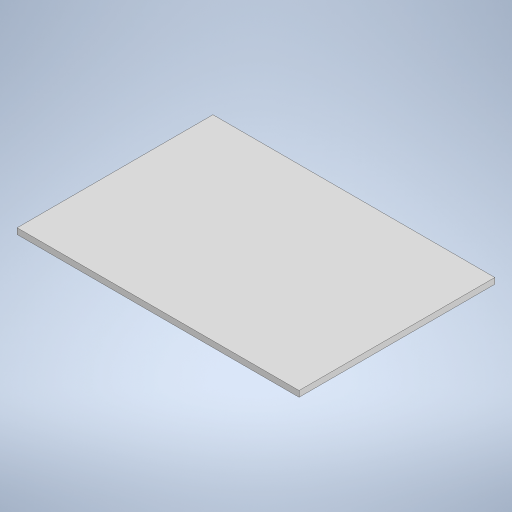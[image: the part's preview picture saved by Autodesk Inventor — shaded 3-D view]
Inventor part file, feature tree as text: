
AUTODESK INVENTOR PART (.ipt)
format: ipt  version: 2024 (Build 280153000, 153)  size: 202,240 bytes
history: native  units: mm
features: other x1, extrude x1, sketch x1
ambient origin geometry x8: Origin, YZ Plane, XZ Plane, XY Plane, X Axis, Y Axis, Z Axis, Center Point
bodies: Body1 (feature_tree)
feature tree (3):
  other  "Sólido1"
  extrude  "Extrusión1"  Depth=50.0mm
  sketch  "Boceto1"  dims[d0=72.0mm d1=50.0mm d2=1.5mm d3=0.0mm]
